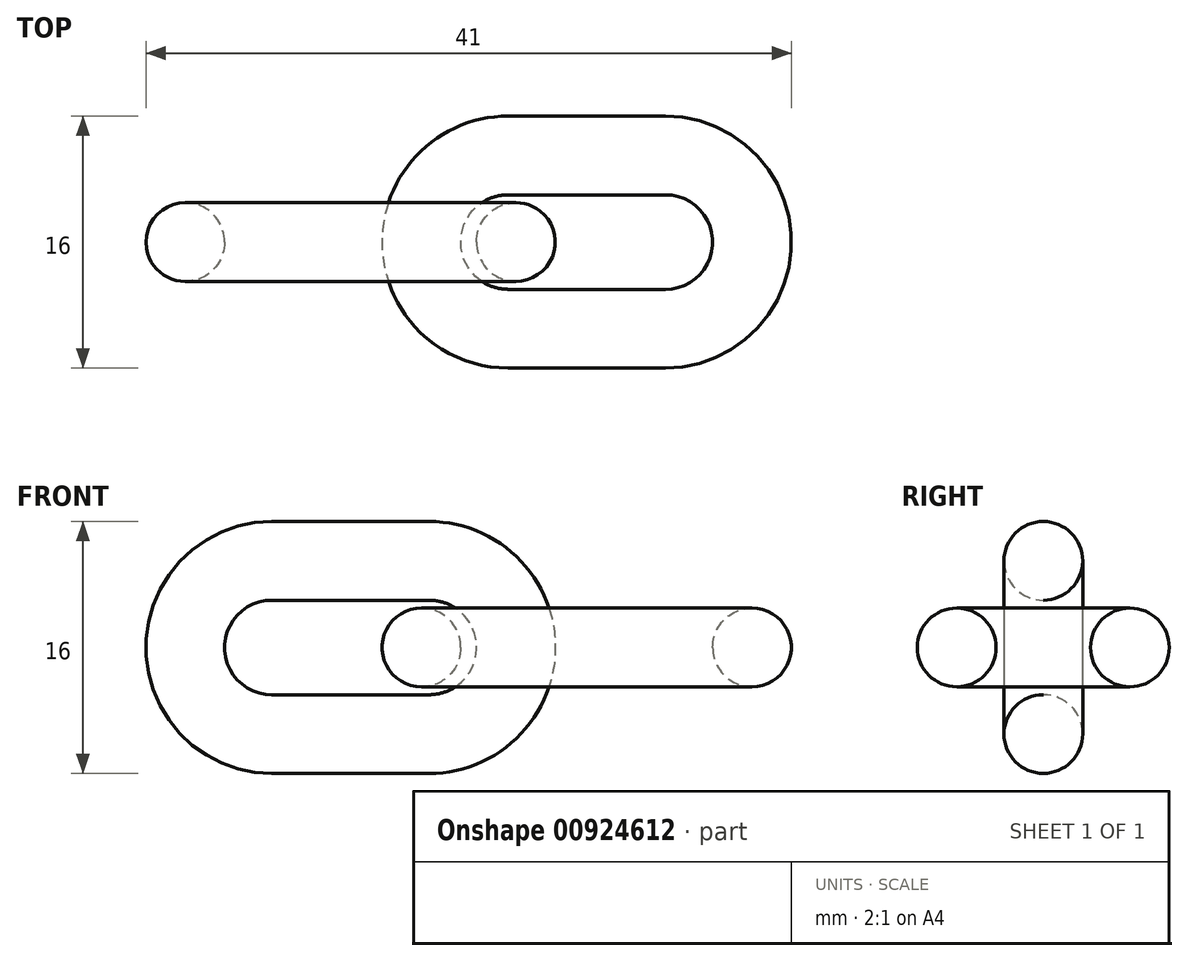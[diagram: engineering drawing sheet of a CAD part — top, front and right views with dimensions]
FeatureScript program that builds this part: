
annotation { "Feature Type Name" : "Feature", "Feature Type Description" : "" }
export const myFeature = defineFeature(function(context is Context, id is Id, definition is map)
    precondition{}
    {
        {
            var Q0;
            Q0=qCreatedBy(makeId("Front.planeOp"),FACE);
            var sketch = newSketch(context, id + "F0", { "sketchPlane" : qUnion([Q0])});
            skLineSegment(sketch, "E0", {"start": v(-10, 5.5) * mm, "end": v(0, 5.5) * mm});
            skLineSegment(sketch, "E1", {"start": v(-10, -5.5) * mm, "end": v(0, -5.5) * mm});
            skLineSegment(sketch, "E2", {"start": v(-10, -5.5) * mm, "end": v(-10, 5.5) * mm});
            skArc(sketch, "E3", {"start": v(-10, 5.5) * mm, "mid": v(-15.5, 0) * mm, "end": v(-10, -5.5) * mm});
            skArc(sketch, "E4", {"start": v(0, -5.5) * mm, "mid": v(5.5, 0) * mm, "end": v(0, 5.5) * mm});
            skLineSegment(sketch, "E5", {"start": v(-10, 0) * mm, "end": v(0, 0) * mm});
            skSolve(sketch);
        }
        {
            var Q0;
            Q0=qCreatedBy(makeId("Right.planeOp"),FACE);
            var sketch = newSketch(context, id + "F1", { "sketchPlane" : qUnion([Q0])});
            skCircle(sketch, "E6", {"center": v(0, 5.5) * mm, "radius": 2.5 * mm});
            skSolve(sketch);
        }
        {
            var Q0;
            Q0=makeQuery(id+"F1.imprint","IMPRINT",FACE,{"disambiguationData":[TD([[makeQuery(id+"F1.imprint","IMPRINT",EDGE,{"derivedFrom":sQuery(id+"F1.wireOp",EDGE,"E6")}),1.0]])]});
            var Q1;
            Q1=sQuery(id+"F0.wireOp",EDGE,"E0");
            var Q2;
            Q2=sQuery(id+"F0.wireOp",EDGE,"E3");
            var Q3;
            Q3=sQuery(id+"F0.wireOp",EDGE,"E1");
            var Q4;
            Q4=sQuery(id+"F0.wireOp",EDGE,"E4");
            sweep(context, id + "F2", {"profiles" : qUnion([Q0]), "path" : qUnion([Q1, Q2, Q3, Q4])});
        }
        {
            var Q0;
            Q0=makeQuery(id+"F2.opSweep","SWEPT_BODY",BODY,{"disambiguationData":[OSD([sQuery(id+"F0.wireOp",EDGE,"E3"),sQuery(id+"F1.wireOp",EDGE,"E6")])]});
            transform(context, id + "F3", {"entities" : qUnion([Q0]), "transformType" : TransformType.TRANSLATION_3D, "dx" : 15 * mm, "dy" : 0 * mm, "dz" : 0 * mm, "makeCopy" : true});
        }
        {
            var Q0;
            Q0=makeQuery(id+"F3.opPattern","COPY",BODY,{"derivedFrom":makeQuery(id+"F2.opSweep","SWEPT_BODY",BODY,{"disambiguationData":[OSD([sQuery(id+"F0.wireOp",EDGE,"E3"),sQuery(id+"F1.wireOp",EDGE,"E6")])]}),"instanceName":"1"});
            var Q1;
            Q1=sQuery(id+"F0.wireOp",EDGE,"E5");
            transform(context, id + "F4", {"entities" : qUnion([Q0]), "transformType" : TransformType.ROTATION, "transformAxis" : qUnion([Q1]), "angle" : 90 * degree, "makeCopy" : false});
        }
    });
